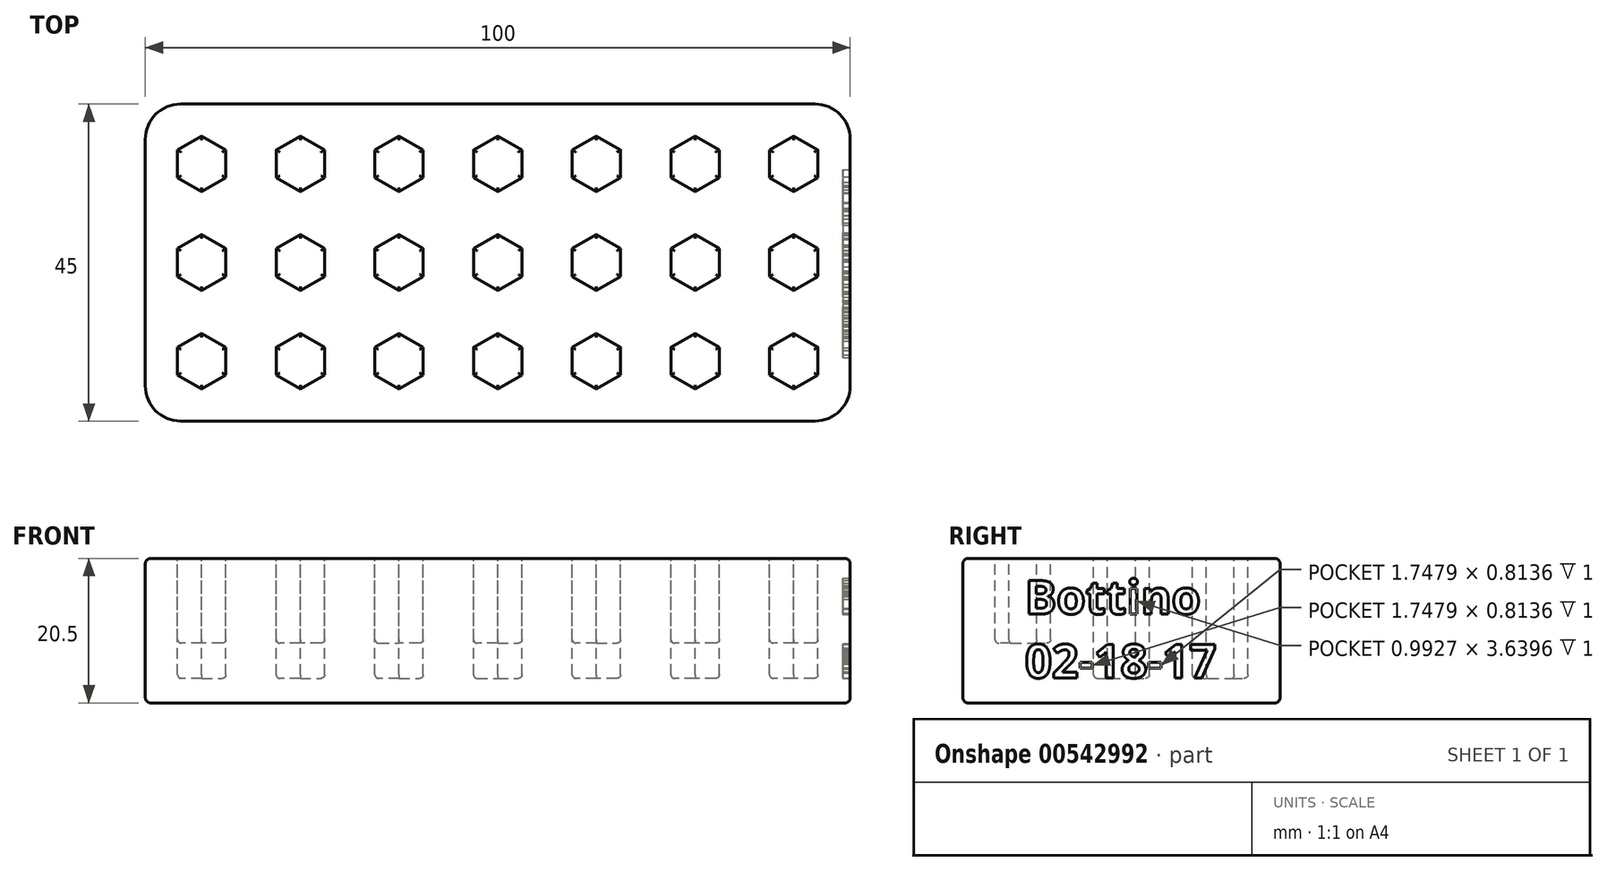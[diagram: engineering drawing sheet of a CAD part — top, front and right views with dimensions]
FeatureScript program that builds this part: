
annotation { "Feature Type Name" : "Feature", "Feature Type Description" : "" }
export const myFeature = defineFeature(function(context is Context, id is Id, definition is map)
    precondition{}
    {
        {
            var Q0;
            Q0=qCreatedBy(makeId("Top.planeOp"),FACE);
            var sketch = newSketch(context, id + "F0", { "sketchPlane" : qUnion([Q0])});
            skLineSegment(sketch, "E0.bottom", {"start": v(45, -22.5) * mm, "end": v(-45, -22.5) * mm});
            skLineSegment(sketch, "E0.top", {"start": v(45, 22.5) * mm, "end": v(-45, 22.5) * mm});
            skLineSegment(sketch, "E0.left", {"start": v(50, -17.5) * mm, "end": v(50, 17.5) * mm});
            skLineSegment(sketch, "E0.right", {"start": v(-50, -17.5) * mm, "end": v(-50, 17.5) * mm});
            skPoint(sketch, "E0.middle", {"position": v(0, 0) * mm});
            skPoint(sketch, "E1.visualSharp", {"position": v(-50, 22.5) * mm});
            skArc(sketch, "E1.filletArc", {"start": v(-45, 22.5) * mm, "mid": v(-48.54, 21.04) * mm, "end": v(-50, 17.5) * mm});
            skPoint(sketch, "E2.visualSharp", {"position": v(50, 22.5) * mm});
            skArc(sketch, "E2.filletArc", {"start": v(50, 17.5) * mm, "mid": v(48.54, 21.04) * mm, "end": v(45, 22.5) * mm});
            skPoint(sketch, "E3.visualSharp", {"position": v(50, -22.5) * mm});
            skArc(sketch, "E3.filletArc", {"start": v(45, -22.5) * mm, "mid": v(48.54, -21.04) * mm, "end": v(50, -17.5) * mm});
            skPoint(sketch, "E4.visualSharp", {"position": v(-50, -22.5) * mm});
            skArc(sketch, "E4.filletArc", {"start": v(-50, -17.5) * mm, "mid": v(-48.54, -21.04) * mm, "end": v(-45, -22.5) * mm});
            skCircle(sketch, "E5.cCircle", {"center": v(0, 0) * mm, "radius": 3.43 * mm, "construction": true});
            skLineSegment(sketch, "E5.0", {"start": v(3.43, 1.98) * mm, "end": v(3.43, -1.98) * mm});
            skLineSegment(sketch, "E5.1", {"start": v(3.43, -1.98) * mm, "end": v(0, -3.95) * mm});
            skLineSegment(sketch, "E5.2", {"start": v(0, -3.95) * mm, "end": v(-3.43, -1.98) * mm});
            skLineSegment(sketch, "E5.3", {"start": v(-3.43, -1.98) * mm, "end": v(-3.43, 1.98) * mm});
            skLineSegment(sketch, "E5.4", {"start": v(-3.43, 1.98) * mm, "end": v(0, 3.95) * mm});
            skLineSegment(sketch, "E5.5", {"start": v(0, 3.95) * mm, "end": v(3.43, 1.98) * mm});
            skPoint(sketch, "E5.0.midPoint", {"position": v(3.43, 0) * mm});
            skLineSegment(sketch, "E6.0.1.0", {"start": v(-3.43, 15.98) * mm, "end": v(0, 17.95) * mm});
            skLineSegment(sketch, "E6.0.1.1", {"start": v(3.43, 12.02) * mm, "end": v(0, 10.05) * mm});
            skLineSegment(sketch, "E6.0.1.2", {"start": v(3.43, 15.98) * mm, "end": v(3.43, 12.02) * mm});
            skPoint(sketch, "E6.0.1.3", {"position": v(3.43, 14) * mm});
            skLineSegment(sketch, "E6.0.1.4", {"start": v(0, 10.05) * mm, "end": v(-3.43, 12.02) * mm});
            skLineSegment(sketch, "E6.0.1.5", {"start": v(-3.43, 12.02) * mm, "end": v(-3.43, 15.98) * mm});
            skCircle(sketch, "E6.0.1.6", {"center": v(0, 14) * mm, "radius": 3.43 * mm, "construction": true});
            skLineSegment(sketch, "E6.0.1.7", {"start": v(0, 17.95) * mm, "end": v(3.43, 15.98) * mm});
            skPoint(sketch, "E6.0.1.8", {"position": v(0, 14) * mm});
            skLineSegment(sketch, "E6.1.0.0", {"start": v(10.58, 1.98) * mm, "end": v(14, 3.95) * mm});
            skLineSegment(sketch, "E6.1.0.1", {"start": v(17.43, -1.98) * mm, "end": v(14, -3.95) * mm});
            skLineSegment(sketch, "E6.1.0.2", {"start": v(17.43, 1.98) * mm, "end": v(17.43, -1.98) * mm});
            skPoint(sketch, "E6.1.0.3", {"position": v(17.43, 0) * mm});
            skLineSegment(sketch, "E6.1.0.4", {"start": v(14, -3.95) * mm, "end": v(10.58, -1.98) * mm});
            skLineSegment(sketch, "E6.1.0.5", {"start": v(10.58, -1.98) * mm, "end": v(10.58, 1.98) * mm});
            skCircle(sketch, "E6.1.0.6", {"center": v(14, 0) * mm, "radius": 3.43 * mm, "construction": true});
            skLineSegment(sketch, "E6.1.0.7", {"start": v(14, 3.95) * mm, "end": v(17.43, 1.98) * mm});
            skPoint(sketch, "E6.1.0.8", {"position": v(14, 0) * mm});
            skLineSegment(sketch, "E6.1.1.0", {"start": v(10.58, 15.98) * mm, "end": v(14, 17.95) * mm});
            skLineSegment(sketch, "E6.1.1.1", {"start": v(17.43, 12.02) * mm, "end": v(14, 10.05) * mm});
            skLineSegment(sketch, "E6.1.1.2", {"start": v(17.43, 15.98) * mm, "end": v(17.43, 12.02) * mm});
            skPoint(sketch, "E6.1.1.3", {"position": v(17.43, 14) * mm});
            skLineSegment(sketch, "E6.1.1.4", {"start": v(14, 10.05) * mm, "end": v(10.58, 12.02) * mm});
            skLineSegment(sketch, "E6.1.1.5", {"start": v(10.58, 12.02) * mm, "end": v(10.58, 15.98) * mm});
            skCircle(sketch, "E6.1.1.6", {"center": v(14, 14) * mm, "radius": 3.43 * mm, "construction": true});
            skLineSegment(sketch, "E6.1.1.7", {"start": v(14, 17.95) * mm, "end": v(17.43, 15.98) * mm});
            skPoint(sketch, "E6.1.1.8", {"position": v(14, 14) * mm});
            skLineSegment(sketch, "E6.2.0.0", {"start": v(24.58, 1.98) * mm, "end": v(28, 3.95) * mm});
            skLineSegment(sketch, "E6.2.0.1", {"start": v(31.43, -1.98) * mm, "end": v(28, -3.95) * mm});
            skLineSegment(sketch, "E6.2.0.2", {"start": v(31.43, 1.98) * mm, "end": v(31.43, -1.98) * mm});
            skPoint(sketch, "E6.2.0.3", {"position": v(31.43, 0) * mm});
            skLineSegment(sketch, "E6.2.0.4", {"start": v(28, -3.95) * mm, "end": v(24.58, -1.98) * mm});
            skLineSegment(sketch, "E6.2.0.5", {"start": v(24.58, -1.98) * mm, "end": v(24.58, 1.98) * mm});
            skCircle(sketch, "E6.2.0.6", {"center": v(28, 0) * mm, "radius": 3.43 * mm, "construction": true});
            skLineSegment(sketch, "E6.2.0.7", {"start": v(28, 3.95) * mm, "end": v(31.43, 1.98) * mm});
            skPoint(sketch, "E6.2.0.8", {"position": v(28, 0) * mm});
            skLineSegment(sketch, "E6.2.1.0", {"start": v(24.58, 15.98) * mm, "end": v(28, 17.95) * mm});
            skLineSegment(sketch, "E6.2.1.1", {"start": v(31.43, 12.02) * mm, "end": v(28, 10.05) * mm});
            skLineSegment(sketch, "E6.2.1.2", {"start": v(31.43, 15.98) * mm, "end": v(31.43, 12.02) * mm});
            skPoint(sketch, "E6.2.1.3", {"position": v(31.43, 14) * mm});
            skLineSegment(sketch, "E6.2.1.4", {"start": v(28, 10.05) * mm, "end": v(24.58, 12.02) * mm});
            skLineSegment(sketch, "E6.2.1.5", {"start": v(24.58, 12.02) * mm, "end": v(24.58, 15.98) * mm});
            skCircle(sketch, "E6.2.1.6", {"center": v(28, 14) * mm, "radius": 3.43 * mm, "construction": true});
            skLineSegment(sketch, "E6.2.1.7", {"start": v(28, 17.95) * mm, "end": v(31.43, 15.98) * mm});
            skPoint(sketch, "E6.2.1.8", {"position": v(28, 14) * mm});
            skLineSegment(sketch, "E6.3.0.0", {"start": v(38.58, 1.98) * mm, "end": v(42, 3.95) * mm});
            skLineSegment(sketch, "E6.3.0.1", {"start": v(45.43, -1.98) * mm, "end": v(42, -3.95) * mm});
            skLineSegment(sketch, "E6.3.0.2", {"start": v(45.43, 1.98) * mm, "end": v(45.43, -1.98) * mm});
            skPoint(sketch, "E6.3.0.3", {"position": v(45.43, 0) * mm});
            skLineSegment(sketch, "E6.3.0.4", {"start": v(42, -3.95) * mm, "end": v(38.58, -1.98) * mm});
            skLineSegment(sketch, "E6.3.0.5", {"start": v(38.58, -1.98) * mm, "end": v(38.58, 1.98) * mm});
            skCircle(sketch, "E6.3.0.6", {"center": v(42, 0) * mm, "radius": 3.43 * mm, "construction": true});
            skLineSegment(sketch, "E6.3.0.7", {"start": v(42, 3.95) * mm, "end": v(45.43, 1.98) * mm});
            skPoint(sketch, "E6.3.0.8", {"position": v(42, 0) * mm});
            skLineSegment(sketch, "E6.3.1.0", {"start": v(38.58, 15.98) * mm, "end": v(42, 17.95) * mm});
            skLineSegment(sketch, "E6.3.1.1", {"start": v(45.43, 12.02) * mm, "end": v(42, 10.05) * mm});
            skLineSegment(sketch, "E6.3.1.2", {"start": v(45.43, 15.98) * mm, "end": v(45.43, 12.02) * mm});
            skPoint(sketch, "E6.3.1.3", {"position": v(45.43, 14) * mm});
            skLineSegment(sketch, "E6.3.1.4", {"start": v(42, 10.05) * mm, "end": v(38.58, 12.02) * mm});
            skLineSegment(sketch, "E6.3.1.5", {"start": v(38.58, 12.02) * mm, "end": v(38.58, 15.98) * mm});
            skCircle(sketch, "E6.3.1.6", {"center": v(42, 14) * mm, "radius": 3.43 * mm, "construction": true});
            skLineSegment(sketch, "E6.3.1.7", {"start": v(42, 17.95) * mm, "end": v(45.43, 15.98) * mm});
            skPoint(sketch, "E6.3.1.8", {"position": v(42, 14) * mm});
            skLineSegment(sketch, "E6.direction1", {"start": v(-3.43, -1.98) * mm, "end": v(10.58, -1.98) * mm, "construction": true});
            skLineSegment(sketch, "E6.direction2", {"start": v(-3.43, -1.98) * mm, "end": v(-3.43, 12.02) * mm, "construction": true});
            skLineSegment(sketch, "E7", {"start": v(0, 36.48) * mm, "end": v(0, -38.23) * mm, "construction": true});
            skLineSegment(sketch, "E8.MirrorCS", {"start": v(-10.58, 15.98) * mm, "end": v(-14, 17.95) * mm});
            skLineSegment(sketch, "E9.MirrorCS", {"start": v(-14, 17.95) * mm, "end": v(-17.43, 15.98) * mm});
            skLineSegment(sketch, "E10.MirrorCS", {"start": v(-17.43, 15.98) * mm, "end": v(-17.43, 12.02) * mm});
            skLineSegment(sketch, "E11.MirrorCS", {"start": v(-17.43, 12.02) * mm, "end": v(-14, 10.05) * mm});
            skLineSegment(sketch, "E12.MirrorCS", {"start": v(-14, 10.05) * mm, "end": v(-10.58, 12.02) * mm});
            skLineSegment(sketch, "E13.MirrorCS", {"start": v(-10.58, 12.02) * mm, "end": v(-10.58, 15.98) * mm});
            skLineSegment(sketch, "E14.MirrorCS", {"start": v(-24.58, 12.02) * mm, "end": v(-24.58, 15.98) * mm});
            skLineSegment(sketch, "E15.MirrorCS", {"start": v(-24.58, 15.98) * mm, "end": v(-28, 17.95) * mm});
            skLineSegment(sketch, "E16.MirrorCS", {"start": v(-28, 17.95) * mm, "end": v(-31.43, 15.98) * mm});
            skLineSegment(sketch, "E17.MirrorCS", {"start": v(-31.43, 15.98) * mm, "end": v(-31.43, 12.02) * mm});
            skLineSegment(sketch, "E18.MirrorCS", {"start": v(-31.43, 12.02) * mm, "end": v(-28, 10.05) * mm});
            skLineSegment(sketch, "E19.MirrorCS", {"start": v(-28, 3.95) * mm, "end": v(-31.43, 1.98) * mm});
            skLineSegment(sketch, "E20.MirrorCS", {"start": v(-24.58, 1.98) * mm, "end": v(-28, 3.95) * mm});
            skLineSegment(sketch, "E21.MirrorCS", {"start": v(-24.58, -1.98) * mm, "end": v(-24.58, 1.98) * mm});
            skLineSegment(sketch, "E22.MirrorCS", {"start": v(-28, -3.95) * mm, "end": v(-24.58, -1.98) * mm});
            skLineSegment(sketch, "E23.MirrorCS", {"start": v(-31.43, -1.98) * mm, "end": v(-28, -3.95) * mm});
            skLineSegment(sketch, "E24.MirrorCS", {"start": v(-28, 10.05) * mm, "end": v(-24.58, 12.02) * mm});
            skLineSegment(sketch, "E25.MirrorCS", {"start": v(-31.43, 1.98) * mm, "end": v(-31.43, -1.98) * mm});
            skLineSegment(sketch, "E26.MirrorCS", {"start": v(-38.58, 15.98) * mm, "end": v(-42, 17.95) * mm});
            skLineSegment(sketch, "E27.MirrorCS", {"start": v(-42, 17.95) * mm, "end": v(-45.43, 15.98) * mm});
            skLineSegment(sketch, "E28.MirrorCS", {"start": v(-45.43, 15.98) * mm, "end": v(-45.43, 12.02) * mm});
            skLineSegment(sketch, "E29.MirrorCS", {"start": v(-45.43, 12.02) * mm, "end": v(-42, 10.05) * mm});
            skLineSegment(sketch, "E30.MirrorCS", {"start": v(-42, 10.05) * mm, "end": v(-38.58, 12.02) * mm});
            skLineSegment(sketch, "E31.MirrorCS", {"start": v(-38.58, 12.02) * mm, "end": v(-38.58, 15.98) * mm});
            skLineSegment(sketch, "E32.MirrorCS", {"start": v(-38.58, 1.98) * mm, "end": v(-42, 3.95) * mm});
            skLineSegment(sketch, "E33.MirrorCS", {"start": v(-42, 3.95) * mm, "end": v(-45.43, 1.98) * mm});
            skLineSegment(sketch, "E34.MirrorCS", {"start": v(-45.43, 1.98) * mm, "end": v(-45.43, -1.98) * mm});
            skLineSegment(sketch, "E35.MirrorCS", {"start": v(-45.43, -1.98) * mm, "end": v(-42, -3.95) * mm});
            skLineSegment(sketch, "E36.MirrorCS", {"start": v(-42, -3.95) * mm, "end": v(-38.58, -1.98) * mm});
            skLineSegment(sketch, "E37.MirrorCS", {"start": v(-38.58, -1.98) * mm, "end": v(-38.58, 1.98) * mm});
            skLineSegment(sketch, "E38.MirrorCS", {"start": v(-10.58, 1.98) * mm, "end": v(-14, 3.95) * mm});
            skLineSegment(sketch, "E39.MirrorCS", {"start": v(-14, 3.95) * mm, "end": v(-17.43, 1.98) * mm});
            skLineSegment(sketch, "E40.MirrorCS", {"start": v(-17.43, 1.98) * mm, "end": v(-17.43, -1.98) * mm});
            skLineSegment(sketch, "E41.MirrorCS", {"start": v(-17.43, -1.98) * mm, "end": v(-14, -3.95) * mm});
            skLineSegment(sketch, "E42.MirrorCS", {"start": v(-14, -3.95) * mm, "end": v(-10.58, -1.98) * mm});
            skLineSegment(sketch, "E43.MirrorCS", {"start": v(-10.58, -1.98) * mm, "end": v(-10.58, 1.98) * mm});
            skLineSegment(sketch, "E44", {"start": v(-62.75, 0) * mm, "end": v(58.2, 0) * mm, "construction": true});
            skLineSegment(sketch, "E45.MirrorCS", {"start": v(-31.43, -12.02) * mm, "end": v(-28, -10.05) * mm});
            skLineSegment(sketch, "E46.MirrorCS", {"start": v(-45.43, -12.02) * mm, "end": v(-42, -10.05) * mm});
            skLineSegment(sketch, "E47.MirrorCS", {"start": v(-28, -17.95) * mm, "end": v(-31.43, -15.98) * mm});
            skLineSegment(sketch, "E48.MirrorCS", {"start": v(-10.58, -15.98) * mm, "end": v(-14, -17.95) * mm});
            skLineSegment(sketch, "E49.MirrorCS", {"start": v(-38.58, -12.02) * mm, "end": v(-38.58, -15.98) * mm});
            skLineSegment(sketch, "E50.MirrorCS", {"start": v(-42, -10.05) * mm, "end": v(-38.58, -12.02) * mm});
            skLineSegment(sketch, "E51.MirrorCS", {"start": v(-31.43, -15.98) * mm, "end": v(-31.43, -12.02) * mm});
            skLineSegment(sketch, "E52.MirrorCS", {"start": v(-45.43, -15.98) * mm, "end": v(-45.43, -12.02) * mm});
            skLineSegment(sketch, "E53.MirrorCS", {"start": v(-24.58, -15.98) * mm, "end": v(-28, -17.95) * mm});
            skLineSegment(sketch, "E54.MirrorCS", {"start": v(-38.58, -15.98) * mm, "end": v(-42, -17.95) * mm});
            skLineSegment(sketch, "E55.MirrorCS", {"start": v(-14, -10.05) * mm, "end": v(-10.58, -12.02) * mm});
            skLineSegment(sketch, "E56.MirrorCS", {"start": v(-10.58, -12.02) * mm, "end": v(-10.58, -15.98) * mm});
            skLineSegment(sketch, "E57.MirrorCS", {"start": v(-28, -10.05) * mm, "end": v(-24.58, -12.02) * mm});
            skLineSegment(sketch, "E58.MirrorCS", {"start": v(-17.43, -12.02) * mm, "end": v(-14, -10.05) * mm});
            skLineSegment(sketch, "E59.MirrorCS", {"start": v(-17.43, -15.98) * mm, "end": v(-17.43, -12.02) * mm});
            skLineSegment(sketch, "E60.MirrorCS", {"start": v(-14, -17.95) * mm, "end": v(-17.43, -15.98) * mm});
            skLineSegment(sketch, "E61.MirrorCS", {"start": v(-42, -17.95) * mm, "end": v(-45.43, -15.98) * mm});
            skLineSegment(sketch, "E62.MirrorCS", {"start": v(-24.58, -12.02) * mm, "end": v(-24.58, -15.98) * mm});
            skLineSegment(sketch, "E63.MirrorCS", {"start": v(-3.43, -15.98) * mm, "end": v(0, -17.95) * mm});
            skLineSegment(sketch, "E64.MirrorCS", {"start": v(0, -17.95) * mm, "end": v(3.43, -15.98) * mm});
            skLineSegment(sketch, "E65.MirrorCS", {"start": v(3.43, -15.98) * mm, "end": v(3.43, -12.02) * mm});
            skLineSegment(sketch, "E66.MirrorCS", {"start": v(3.43, -12.02) * mm, "end": v(0, -10.05) * mm});
            skLineSegment(sketch, "E67.MirrorCS", {"start": v(0, -10.05) * mm, "end": v(-3.43, -12.02) * mm});
            skLineSegment(sketch, "E68.MirrorCS", {"start": v(-3.43, -12.02) * mm, "end": v(-3.43, -15.98) * mm});
            skLineSegment(sketch, "E69.MirrorCS", {"start": v(10.58, -15.98) * mm, "end": v(14, -17.95) * mm});
            skLineSegment(sketch, "E70.MirrorCS", {"start": v(14, -17.95) * mm, "end": v(17.43, -15.98) * mm});
            skLineSegment(sketch, "E71.MirrorCS", {"start": v(17.43, -15.98) * mm, "end": v(17.43, -12.02) * mm});
            skLineSegment(sketch, "E72.MirrorCS", {"start": v(17.43, -12.02) * mm, "end": v(14, -10.05) * mm});
            skLineSegment(sketch, "E73.MirrorCS", {"start": v(14, -10.05) * mm, "end": v(10.58, -12.02) * mm});
            skLineSegment(sketch, "E74.MirrorCS", {"start": v(10.58, -12.02) * mm, "end": v(10.58, -15.98) * mm});
            skLineSegment(sketch, "E75.MirrorCS", {"start": v(28, -10.05) * mm, "end": v(24.58, -12.02) * mm});
            skLineSegment(sketch, "E76.MirrorCS", {"start": v(24.58, -12.02) * mm, "end": v(24.58, -15.98) * mm});
            skLineSegment(sketch, "E77.MirrorCS", {"start": v(24.58, -15.98) * mm, "end": v(28, -17.95) * mm});
            skLineSegment(sketch, "E78.MirrorCS", {"start": v(28, -17.95) * mm, "end": v(31.43, -15.98) * mm});
            skLineSegment(sketch, "E79.MirrorCS", {"start": v(31.43, -15.98) * mm, "end": v(31.43, -12.02) * mm});
            skLineSegment(sketch, "E80.MirrorCS", {"start": v(31.43, -12.02) * mm, "end": v(28, -10.05) * mm});
            skLineSegment(sketch, "E81.MirrorCS", {"start": v(42, -10.05) * mm, "end": v(38.58, -12.02) * mm});
            skLineSegment(sketch, "E82.MirrorCS", {"start": v(38.58, -12.02) * mm, "end": v(38.58, -15.98) * mm});
            skLineSegment(sketch, "E83.MirrorCS", {"start": v(38.58, -15.98) * mm, "end": v(42, -17.95) * mm});
            skLineSegment(sketch, "E84.MirrorCS", {"start": v(42, -17.95) * mm, "end": v(45.43, -15.98) * mm});
            skLineSegment(sketch, "E85.MirrorCS", {"start": v(45.43, -15.98) * mm, "end": v(45.43, -12.02) * mm});
            skLineSegment(sketch, "E86.MirrorCS", {"start": v(45.43, -12.02) * mm, "end": v(42, -10.05) * mm});
            skSolve(sketch);
        }
        {
            var Q0;
            Q0=qCreatedBy(makeId("Top.planeOp"),FACE);
            var sketch = newSketch(context, id + "F1", { "sketchPlane" : qUnion([Q0])});
            skArc(sketch, "E87.0", {"start": v(-45, 22.5) * mm, "mid": v(-48.54, 21.04) * mm, "end": v(-50, 17.5) * mm});
            skLineSegment(sketch, "E88.0", {"start": v(45, 22.5) * mm, "end": v(-45, 22.5) * mm});
            skArc(sketch, "E89.0", {"start": v(50, 17.5) * mm, "mid": v(48.54, 21.04) * mm, "end": v(45, 22.5) * mm});
            skLineSegment(sketch, "E90.0", {"start": v(50, -17.5) * mm, "end": v(50, 17.5) * mm});
            skArc(sketch, "E91.0", {"start": v(45, -22.5) * mm, "mid": v(48.54, -21.04) * mm, "end": v(50, -17.5) * mm});
            skLineSegment(sketch, "E92.0", {"start": v(45, -22.5) * mm, "end": v(-45, -22.5) * mm});
            skArc(sketch, "E93.0", {"start": v(-50, -17.5) * mm, "mid": v(-48.54, -21.04) * mm, "end": v(-45, -22.5) * mm});
            skLineSegment(sketch, "E94.0", {"start": v(-50, -17.5) * mm, "end": v(-50, 17.5) * mm});
            skSolve(sketch);
        }
        {
            var Q0;
            Q0 = qSketchRegion(id + "F1", true);
            extrude(context, id + "F2", {"entities" : qUnion([Q0]), "oppositeDirection" : true, "depth" : 20.5 * mm, "offsetDistance" : 25 * mm});
        }
        {
            var Q0;
            Q0=makeQuery(id+"F0.imprint","IMPRINT",FACE,{"disambiguationData":[TD([[makeQuery(id+"F0.imprint","IMPRINT",EDGE,{"derivedFrom":sQuery(id+"F0.wireOp",EDGE,"E46.MirrorCS")}),-1.0]])]});
            var Q1;
            Q1=makeQuery(id+"F0.imprint","IMPRINT",FACE,{"disambiguationData":[TD([[makeQuery(id+"F0.imprint","IMPRINT",EDGE,{"derivedFrom":sQuery(id+"F0.wireOp",EDGE,"E47.MirrorCS")}),-1.0]])]});
            var Q2;
            Q2=makeQuery(id+"F0.imprint","IMPRINT",FACE,{"disambiguationData":[TD([[makeQuery(id+"F0.imprint","IMPRINT",EDGE,{"derivedFrom":sQuery(id+"F0.wireOp",EDGE,"E48.MirrorCS")}),-1.0]])]});
            var Q3;
            Q3=makeQuery(id+"F0.imprint","IMPRINT",FACE,{"disambiguationData":[TD([[makeQuery(id+"F0.imprint","IMPRINT",EDGE,{"derivedFrom":sQuery(id+"F0.wireOp",EDGE,"E63.MirrorCS")}),1.0]])]});
            var Q4;
            Q4=makeQuery(id+"F0.imprint","IMPRINT",FACE,{"disambiguationData":[TD([[makeQuery(id+"F0.imprint","IMPRINT",EDGE,{"derivedFrom":sQuery(id+"F0.wireOp",EDGE,"E69.MirrorCS")}),1.0]])]});
            var Q5;
            Q5=makeQuery(id+"F0.imprint","IMPRINT",FACE,{"disambiguationData":[TD([[makeQuery(id+"F0.imprint","IMPRINT",EDGE,{"derivedFrom":sQuery(id+"F0.wireOp",EDGE,"E75.MirrorCS")}),1.0]])]});
            var Q6;
            Q6=makeQuery(id+"F0.imprint","IMPRINT",FACE,{"disambiguationData":[TD([[makeQuery(id+"F0.imprint","IMPRINT",EDGE,{"derivedFrom":sQuery(id+"F0.wireOp",EDGE,"E81.MirrorCS")}),1.0]])]});
            extrude(context, id + "F3", {"entities" : qUnion([Q0, Q1, Q2, Q3, Q4, Q5, Q6]), "operationType" : NewBodyOperationType.REMOVE, "oppositeDirection" : true, "depth" : 12 * mm, "offsetDistance" : 25 * mm});
        }
        {
            var Q0;
            Q0=makeQuery(id+"F0.imprint","IMPRINT",FACE,{"disambiguationData":[TD([[makeQuery(id+"F0.imprint","IMPRINT",EDGE,{"derivedFrom":sQuery(id+"F0.wireOp",EDGE,"E26.MirrorCS")}),1.0]])]});
            var Q1;
            Q1=makeQuery(id+"F0.imprint","IMPRINT",FACE,{"disambiguationData":[TD([[makeQuery(id+"F0.imprint","IMPRINT",EDGE,{"derivedFrom":sQuery(id+"F0.wireOp",EDGE,"E14.MirrorCS")}),1.0]])]});
            var Q2;
            Q2=makeQuery(id+"F0.imprint","IMPRINT",FACE,{"disambiguationData":[TD([[makeQuery(id+"F0.imprint","IMPRINT",EDGE,{"derivedFrom":sQuery(id+"F0.wireOp",EDGE,"E8.MirrorCS")}),1.0]])]});
            var Q3;
            Q3=makeQuery(id+"F0.imprint","IMPRINT",FACE,{"disambiguationData":[TD([[makeQuery(id+"F0.imprint","IMPRINT",EDGE,{"derivedFrom":sQuery(id+"F0.wireOp",EDGE,"E6.0.1.0")}),-1.0]])]});
            var Q4;
            Q4=makeQuery(id+"F0.imprint","IMPRINT",FACE,{"disambiguationData":[TD([[makeQuery(id+"F0.imprint","IMPRINT",EDGE,{"derivedFrom":sQuery(id+"F0.wireOp",EDGE,"E6.1.1.0")}),-1.0]])]});
            var Q5;
            Q5=makeQuery(id+"F0.imprint","IMPRINT",FACE,{"disambiguationData":[TD([[makeQuery(id+"F0.imprint","IMPRINT",EDGE,{"derivedFrom":sQuery(id+"F0.wireOp",EDGE,"E6.2.1.0")}),-1.0]])]});
            var Q6;
            Q6=makeQuery(id+"F0.imprint","IMPRINT",FACE,{"disambiguationData":[TD([[makeQuery(id+"F0.imprint","IMPRINT",EDGE,{"derivedFrom":sQuery(id+"F0.wireOp",EDGE,"E6.3.1.0")}),-1.0]])]});
            var Q7;
            Q7=makeQuery(id+"F0.imprint","IMPRINT",FACE,{"disambiguationData":[TD([[makeQuery(id+"F0.imprint","IMPRINT",EDGE,{"derivedFrom":sQuery(id+"F0.wireOp",EDGE,"E6.3.0.0")}),-1.0]])]});
            var Q8;
            Q8=makeQuery(id+"F0.imprint","IMPRINT",FACE,{"disambiguationData":[TD([[makeQuery(id+"F0.imprint","IMPRINT",EDGE,{"derivedFrom":sQuery(id+"F0.wireOp",EDGE,"E6.2.0.0")}),-1.0]])]});
            var Q9;
            Q9=makeQuery(id+"F0.imprint","IMPRINT",FACE,{"disambiguationData":[TD([[makeQuery(id+"F0.imprint","IMPRINT",EDGE,{"derivedFrom":sQuery(id+"F0.wireOp",EDGE,"E6.1.0.0")}),-1.0]])]});
            var Q10;
            Q10=makeQuery(id+"F0.imprint","IMPRINT",FACE,{"disambiguationData":[TD([[makeQuery(id+"F0.imprint","IMPRINT",EDGE,{"derivedFrom":sQuery(id+"F0.wireOp",EDGE,"E5.0")}),-1.0]])]});
            var Q11;
            Q11=makeQuery(id+"F0.imprint","IMPRINT",FACE,{"disambiguationData":[TD([[makeQuery(id+"F0.imprint","IMPRINT",EDGE,{"derivedFrom":sQuery(id+"F0.wireOp",EDGE,"E38.MirrorCS")}),1.0]])]});
            var Q12;
            Q12=makeQuery(id+"F0.imprint","IMPRINT",FACE,{"disambiguationData":[TD([[makeQuery(id+"F0.imprint","IMPRINT",EDGE,{"derivedFrom":sQuery(id+"F0.wireOp",EDGE,"E19.MirrorCS")}),1.0]])]});
            var Q13;
            Q13=makeQuery(id+"F0.imprint","IMPRINT",FACE,{"disambiguationData":[TD([[makeQuery(id+"F0.imprint","IMPRINT",EDGE,{"derivedFrom":sQuery(id+"F0.wireOp",EDGE,"E32.MirrorCS")}),1.0]])]});
            extrude(context, id + "F4", {"entities" : qUnion([Q0, Q1, Q2, Q3, Q4, Q5, Q6, Q7, Q8, Q9, Q10, Q11, Q12, Q13]), "operationType" : NewBodyOperationType.REMOVE, "oppositeDirection" : true, "depth" : 17 * mm, "offsetDistance" : 25 * mm});
        }
        {
            var Q0;
            Q0=makeQuery(id+"F4.boolean.opBoolean","COPY",FACE,{"derivedFrom":makeQuery(id+"F4.opExtrude","CAP_FACE",FACE,{"disambiguationData":[OSD([sQuery(id+"F0.wireOp",EDGE,"E26.MirrorCS"),sQuery(id+"F0.wireOp",EDGE,"E27.MirrorCS"),sQuery(id+"F0.wireOp",EDGE,"E28.MirrorCS"),sQuery(id+"F0.wireOp",EDGE,"E29.MirrorCS"),sQuery(id+"F0.wireOp",EDGE,"E30.MirrorCS"),sQuery(id+"F0.wireOp",EDGE,"E31.MirrorCS")])],"isStart":false})});
            var Q1;
            Q1=makeQuery(id+"F4.boolean.opBoolean","COPY",FACE,{"derivedFrom":makeQuery(id+"F4.opExtrude","CAP_FACE",FACE,{"disambiguationData":[OSD([sQuery(id+"F0.wireOp",EDGE,"E14.MirrorCS"),sQuery(id+"F0.wireOp",EDGE,"E15.MirrorCS"),sQuery(id+"F0.wireOp",EDGE,"E16.MirrorCS"),sQuery(id+"F0.wireOp",EDGE,"E17.MirrorCS"),sQuery(id+"F0.wireOp",EDGE,"E18.MirrorCS"),sQuery(id+"F0.wireOp",EDGE,"E24.MirrorCS")])],"isStart":false})});
            var Q2;
            Q2=makeQuery(id+"F4.boolean.opBoolean","COPY",FACE,{"derivedFrom":makeQuery(id+"F4.opExtrude","CAP_FACE",FACE,{"disambiguationData":[OSD([sQuery(id+"F0.wireOp",EDGE,"E8.MirrorCS"),sQuery(id+"F0.wireOp",EDGE,"E9.MirrorCS"),sQuery(id+"F0.wireOp",EDGE,"E10.MirrorCS"),sQuery(id+"F0.wireOp",EDGE,"E11.MirrorCS"),sQuery(id+"F0.wireOp",EDGE,"E12.MirrorCS"),sQuery(id+"F0.wireOp",EDGE,"E13.MirrorCS")])],"isStart":false})});
            var Q3;
            Q3=makeQuery(id+"F4.boolean.opBoolean","COPY",FACE,{"derivedFrom":makeQuery(id+"F4.opExtrude","CAP_FACE",FACE,{"disambiguationData":[OSD([sQuery(id+"F0.wireOp",EDGE,"E6.0.1.0"),sQuery(id+"F0.wireOp",EDGE,"E6.0.1.1"),sQuery(id+"F0.wireOp",EDGE,"E6.0.1.2"),sQuery(id+"F0.wireOp",EDGE,"E6.0.1.4"),sQuery(id+"F0.wireOp",EDGE,"E6.0.1.5"),sQuery(id+"F0.wireOp",EDGE,"E6.0.1.7")])],"isStart":false})});
            var Q4;
            Q4=makeQuery(id+"F4.boolean.opBoolean","COPY",FACE,{"derivedFrom":makeQuery(id+"F4.opExtrude","CAP_FACE",FACE,{"disambiguationData":[OSD([sQuery(id+"F0.wireOp",EDGE,"E6.1.1.0"),sQuery(id+"F0.wireOp",EDGE,"E6.1.1.1"),sQuery(id+"F0.wireOp",EDGE,"E6.1.1.2"),sQuery(id+"F0.wireOp",EDGE,"E6.1.1.4"),sQuery(id+"F0.wireOp",EDGE,"E6.1.1.5"),sQuery(id+"F0.wireOp",EDGE,"E6.1.1.7")])],"isStart":false})});
            var Q5;
            Q5=makeQuery(id+"F4.boolean.opBoolean","COPY",FACE,{"derivedFrom":makeQuery(id+"F4.opExtrude","CAP_FACE",FACE,{"disambiguationData":[OSD([sQuery(id+"F0.wireOp",EDGE,"E6.2.1.0"),sQuery(id+"F0.wireOp",EDGE,"E6.2.1.1"),sQuery(id+"F0.wireOp",EDGE,"E6.2.1.2"),sQuery(id+"F0.wireOp",EDGE,"E6.2.1.4"),sQuery(id+"F0.wireOp",EDGE,"E6.2.1.5"),sQuery(id+"F0.wireOp",EDGE,"E6.2.1.7")])],"isStart":false})});
            var Q6;
            Q6=makeQuery(id+"F4.boolean.opBoolean","COPY",FACE,{"derivedFrom":makeQuery(id+"F4.opExtrude","CAP_FACE",FACE,{"disambiguationData":[OSD([sQuery(id+"F0.wireOp",EDGE,"E6.3.1.0"),sQuery(id+"F0.wireOp",EDGE,"E6.3.1.1"),sQuery(id+"F0.wireOp",EDGE,"E6.3.1.2"),sQuery(id+"F0.wireOp",EDGE,"E6.3.1.4"),sQuery(id+"F0.wireOp",EDGE,"E6.3.1.5"),sQuery(id+"F0.wireOp",EDGE,"E6.3.1.7")])],"isStart":false})});
            var Q7;
            Q7=makeQuery(id+"F4.boolean.opBoolean","COPY",FACE,{"derivedFrom":makeQuery(id+"F4.opExtrude","CAP_FACE",FACE,{"disambiguationData":[OSD([sQuery(id+"F0.wireOp",EDGE,"E6.3.0.0"),sQuery(id+"F0.wireOp",EDGE,"E6.3.0.1"),sQuery(id+"F0.wireOp",EDGE,"E6.3.0.2"),sQuery(id+"F0.wireOp",EDGE,"E6.3.0.4"),sQuery(id+"F0.wireOp",EDGE,"E6.3.0.5"),sQuery(id+"F0.wireOp",EDGE,"E6.3.0.7")])],"isStart":false})});
            var Q8;
            Q8=makeQuery(id+"F4.boolean.opBoolean","COPY",FACE,{"derivedFrom":makeQuery(id+"F4.opExtrude","CAP_FACE",FACE,{"disambiguationData":[OSD([sQuery(id+"F0.wireOp",EDGE,"E6.2.0.0"),sQuery(id+"F0.wireOp",EDGE,"E6.2.0.1"),sQuery(id+"F0.wireOp",EDGE,"E6.2.0.2"),sQuery(id+"F0.wireOp",EDGE,"E6.2.0.4"),sQuery(id+"F0.wireOp",EDGE,"E6.2.0.5"),sQuery(id+"F0.wireOp",EDGE,"E6.2.0.7")])],"isStart":false})});
            var Q9;
            Q9=makeQuery(id+"F4.boolean.opBoolean","COPY",FACE,{"derivedFrom":makeQuery(id+"F4.opExtrude","CAP_FACE",FACE,{"disambiguationData":[OSD([sQuery(id+"F0.wireOp",EDGE,"E6.1.0.0"),sQuery(id+"F0.wireOp",EDGE,"E6.1.0.1"),sQuery(id+"F0.wireOp",EDGE,"E6.1.0.2"),sQuery(id+"F0.wireOp",EDGE,"E6.1.0.4"),sQuery(id+"F0.wireOp",EDGE,"E6.1.0.5"),sQuery(id+"F0.wireOp",EDGE,"E6.1.0.7")])],"isStart":false})});
            var Q10;
            Q10=makeQuery(id+"F4.boolean.opBoolean","COPY",FACE,{"derivedFrom":makeQuery(id+"F4.opExtrude","CAP_FACE",FACE,{"disambiguationData":[OSD([sQuery(id+"F0.wireOp",EDGE,"E5.0"),sQuery(id+"F0.wireOp",EDGE,"E5.1"),sQuery(id+"F0.wireOp",EDGE,"E5.2"),sQuery(id+"F0.wireOp",EDGE,"E5.3"),sQuery(id+"F0.wireOp",EDGE,"E5.4"),sQuery(id+"F0.wireOp",EDGE,"E5.5")])],"isStart":false})});
            var Q11;
            Q11=makeQuery(id+"F4.boolean.opBoolean","COPY",FACE,{"derivedFrom":makeQuery(id+"F4.opExtrude","CAP_FACE",FACE,{"disambiguationData":[OSD([sQuery(id+"F0.wireOp",EDGE,"E38.MirrorCS"),sQuery(id+"F0.wireOp",EDGE,"E39.MirrorCS"),sQuery(id+"F0.wireOp",EDGE,"E40.MirrorCS"),sQuery(id+"F0.wireOp",EDGE,"E41.MirrorCS"),sQuery(id+"F0.wireOp",EDGE,"E42.MirrorCS"),sQuery(id+"F0.wireOp",EDGE,"E43.MirrorCS")])],"isStart":false})});
            var Q12;
            Q12=makeQuery(id+"F4.boolean.opBoolean","COPY",FACE,{"derivedFrom":makeQuery(id+"F4.opExtrude","CAP_FACE",FACE,{"disambiguationData":[OSD([sQuery(id+"F0.wireOp",EDGE,"E19.MirrorCS"),sQuery(id+"F0.wireOp",EDGE,"E20.MirrorCS"),sQuery(id+"F0.wireOp",EDGE,"E22.MirrorCS"),sQuery(id+"F0.wireOp",EDGE,"E23.MirrorCS"),sQuery(id+"F0.wireOp",EDGE,"E21.MirrorCS"),sQuery(id+"F0.wireOp",EDGE,"E25.MirrorCS")])],"isStart":false})});
            var Q13;
            Q13=makeQuery(id+"F4.boolean.opBoolean","COPY",FACE,{"derivedFrom":makeQuery(id+"F4.opExtrude","CAP_FACE",FACE,{"disambiguationData":[OSD([sQuery(id+"F0.wireOp",EDGE,"E32.MirrorCS"),sQuery(id+"F0.wireOp",EDGE,"E33.MirrorCS"),sQuery(id+"F0.wireOp",EDGE,"E34.MirrorCS"),sQuery(id+"F0.wireOp",EDGE,"E35.MirrorCS"),sQuery(id+"F0.wireOp",EDGE,"E36.MirrorCS"),sQuery(id+"F0.wireOp",EDGE,"E37.MirrorCS")])],"isStart":false})});
            var Q14;
            Q14=makeQuery(id+"F3.boolean.opBoolean","COPY",FACE,{"derivedFrom":makeQuery(id+"F3.opExtrude","CAP_FACE",FACE,{"disambiguationData":[OSD([sQuery(id+"F0.wireOp",EDGE,"E46.MirrorCS"),sQuery(id+"F0.wireOp",EDGE,"E49.MirrorCS"),sQuery(id+"F0.wireOp",EDGE,"E50.MirrorCS"),sQuery(id+"F0.wireOp",EDGE,"E52.MirrorCS"),sQuery(id+"F0.wireOp",EDGE,"E54.MirrorCS"),sQuery(id+"F0.wireOp",EDGE,"E61.MirrorCS")])],"isStart":false})});
            var Q15;
            Q15=makeQuery(id+"F3.boolean.opBoolean","COPY",FACE,{"derivedFrom":makeQuery(id+"F3.opExtrude","CAP_FACE",FACE,{"disambiguationData":[OSD([sQuery(id+"F0.wireOp",EDGE,"E47.MirrorCS"),sQuery(id+"F0.wireOp",EDGE,"E51.MirrorCS"),sQuery(id+"F0.wireOp",EDGE,"E45.MirrorCS"),sQuery(id+"F0.wireOp",EDGE,"E53.MirrorCS"),sQuery(id+"F0.wireOp",EDGE,"E57.MirrorCS"),sQuery(id+"F0.wireOp",EDGE,"E62.MirrorCS")])],"isStart":false})});
            var Q16;
            Q16=makeQuery(id+"F3.boolean.opBoolean","COPY",FACE,{"derivedFrom":makeQuery(id+"F3.opExtrude","CAP_FACE",FACE,{"disambiguationData":[OSD([sQuery(id+"F0.wireOp",EDGE,"E48.MirrorCS"),sQuery(id+"F0.wireOp",EDGE,"E55.MirrorCS"),sQuery(id+"F0.wireOp",EDGE,"E56.MirrorCS"),sQuery(id+"F0.wireOp",EDGE,"E58.MirrorCS"),sQuery(id+"F0.wireOp",EDGE,"E59.MirrorCS"),sQuery(id+"F0.wireOp",EDGE,"E60.MirrorCS")])],"isStart":false})});
            var Q17;
            Q17=makeQuery(id+"F3.boolean.opBoolean","COPY",FACE,{"derivedFrom":makeQuery(id+"F3.opExtrude","CAP_FACE",FACE,{"disambiguationData":[OSD([sQuery(id+"F0.wireOp",EDGE,"E63.MirrorCS"),sQuery(id+"F0.wireOp",EDGE,"E64.MirrorCS"),sQuery(id+"F0.wireOp",EDGE,"E65.MirrorCS"),sQuery(id+"F0.wireOp",EDGE,"E66.MirrorCS"),sQuery(id+"F0.wireOp",EDGE,"E67.MirrorCS"),sQuery(id+"F0.wireOp",EDGE,"E68.MirrorCS")])],"isStart":false})});
            var Q18;
            Q18=makeQuery(id+"F3.boolean.opBoolean","COPY",FACE,{"derivedFrom":makeQuery(id+"F3.opExtrude","CAP_FACE",FACE,{"disambiguationData":[OSD([sQuery(id+"F0.wireOp",EDGE,"E69.MirrorCS"),sQuery(id+"F0.wireOp",EDGE,"E70.MirrorCS"),sQuery(id+"F0.wireOp",EDGE,"E71.MirrorCS"),sQuery(id+"F0.wireOp",EDGE,"E72.MirrorCS"),sQuery(id+"F0.wireOp",EDGE,"E73.MirrorCS"),sQuery(id+"F0.wireOp",EDGE,"E74.MirrorCS")])],"isStart":false})});
            var Q19;
            Q19=makeQuery(id+"F3.boolean.opBoolean","COPY",FACE,{"derivedFrom":makeQuery(id+"F3.opExtrude","CAP_FACE",FACE,{"disambiguationData":[OSD([sQuery(id+"F0.wireOp",EDGE,"E75.MirrorCS"),sQuery(id+"F0.wireOp",EDGE,"E76.MirrorCS"),sQuery(id+"F0.wireOp",EDGE,"E77.MirrorCS"),sQuery(id+"F0.wireOp",EDGE,"E78.MirrorCS"),sQuery(id+"F0.wireOp",EDGE,"E79.MirrorCS"),sQuery(id+"F0.wireOp",EDGE,"E80.MirrorCS")])],"isStart":false})});
            var Q20;
            Q20=makeQuery(id+"F3.boolean.opBoolean","COPY",FACE,{"derivedFrom":makeQuery(id+"F3.opExtrude","CAP_FACE",FACE,{"disambiguationData":[OSD([sQuery(id+"F0.wireOp",EDGE,"E81.MirrorCS"),sQuery(id+"F0.wireOp",EDGE,"E82.MirrorCS"),sQuery(id+"F0.wireOp",EDGE,"E83.MirrorCS"),sQuery(id+"F0.wireOp",EDGE,"E84.MirrorCS"),sQuery(id+"F0.wireOp",EDGE,"E85.MirrorCS"),sQuery(id+"F0.wireOp",EDGE,"E86.MirrorCS")])],"isStart":false})});
            fillet(context, id + "F5", {"entities" : qUnion([Q0, Q1, Q2, Q3, Q4, Q5, Q6, Q7, Q8, Q9, Q10, Q11, Q12, Q13, Q14, Q15, Q16, Q17, Q18, Q19, Q20]), "radius" : .5 * mm, "tangentPropagation" : true, "allowEdgeOverflow" : false});
        }
        {
            var Q0;
            Q0=makeQuery(id+"F4.boolean.opBoolean","COPY",EDGE,{"derivedFrom":makeQuery(id+"F4.opExtrude","CAP_EDGE",EDGE,{"disambiguationData":[OSD([sQuery(id+"F0.wireOp",EDGE,"E27.MirrorCS")])],"isStart":true})});
            var Q1;
            Q1=makeQuery(id+"F4.boolean.opBoolean","COPY",EDGE,{"derivedFrom":makeQuery(id+"F4.opExtrude","CAP_EDGE",EDGE,{"disambiguationData":[OSD([sQuery(id+"F0.wireOp",EDGE,"E26.MirrorCS")])],"isStart":true})});
            var Q2;
            Q2=makeQuery(id+"F4.boolean.opBoolean","COPY",EDGE,{"derivedFrom":makeQuery(id+"F4.opExtrude","CAP_EDGE",EDGE,{"disambiguationData":[OSD([sQuery(id+"F0.wireOp",EDGE,"E31.MirrorCS")])],"isStart":true})});
            var Q3;
            Q3=makeQuery(id+"F4.boolean.opBoolean","COPY",EDGE,{"derivedFrom":makeQuery(id+"F4.opExtrude","CAP_EDGE",EDGE,{"disambiguationData":[OSD([sQuery(id+"F0.wireOp",EDGE,"E30.MirrorCS")])],"isStart":true})});
            var Q4;
            Q4=makeQuery(id+"F4.boolean.opBoolean","COPY",EDGE,{"derivedFrom":makeQuery(id+"F4.opExtrude","CAP_EDGE",EDGE,{"disambiguationData":[OSD([sQuery(id+"F0.wireOp",EDGE,"E29.MirrorCS")])],"isStart":true})});
            var Q5;
            Q5=makeQuery(id+"F4.boolean.opBoolean","COPY",EDGE,{"derivedFrom":makeQuery(id+"F4.opExtrude","CAP_EDGE",EDGE,{"disambiguationData":[OSD([sQuery(id+"F0.wireOp",EDGE,"E28.MirrorCS")])],"isStart":true})});
            var Q6;
            Q6=makeQuery(id+"F4.boolean.opBoolean","COPY",EDGE,{"derivedFrom":makeQuery(id+"F4.opExtrude","CAP_EDGE",EDGE,{"disambiguationData":[OSD([sQuery(id+"F0.wireOp",EDGE,"E33.MirrorCS")])],"isStart":true})});
            var Q7;
            Q7=makeQuery(id+"F4.boolean.opBoolean","COPY",EDGE,{"derivedFrom":makeQuery(id+"F4.opExtrude","CAP_EDGE",EDGE,{"disambiguationData":[OSD([sQuery(id+"F0.wireOp",EDGE,"E37.MirrorCS")])],"isStart":true})});
            var Q8;
            Q8=makeQuery(id+"F4.boolean.opBoolean","COPY",EDGE,{"derivedFrom":makeQuery(id+"F4.opExtrude","CAP_EDGE",EDGE,{"disambiguationData":[OSD([sQuery(id+"F0.wireOp",EDGE,"E35.MirrorCS")])],"isStart":true})});
            var Q9;
            Q9=makeQuery(id+"F4.boolean.opBoolean","COPY",EDGE,{"derivedFrom":makeQuery(id+"F4.opExtrude","CAP_EDGE",EDGE,{"disambiguationData":[OSD([sQuery(id+"F0.wireOp",EDGE,"E34.MirrorCS")])],"isStart":true})});
            var Q10;
            Q10=makeQuery(id+"F4.boolean.opBoolean","COPY",EDGE,{"derivedFrom":makeQuery(id+"F4.opExtrude","CAP_EDGE",EDGE,{"disambiguationData":[OSD([sQuery(id+"F0.wireOp",EDGE,"E32.MirrorCS")])],"isStart":true})});
            var Q11;
            Q11=makeQuery(id+"F4.boolean.opBoolean","COPY",EDGE,{"derivedFrom":makeQuery(id+"F4.opExtrude","CAP_EDGE",EDGE,{"disambiguationData":[OSD([sQuery(id+"F0.wireOp",EDGE,"E36.MirrorCS")])],"isStart":true})});
            var Q12;
            Q12=makeQuery(id+"F3.boolean.opBoolean","COPY",EDGE,{"derivedFrom":makeQuery(id+"F3.opExtrude","CAP_EDGE",EDGE,{"disambiguationData":[OSD([sQuery(id+"F0.wireOp",EDGE,"E61.MirrorCS")])],"isStart":true})});
            var Q13;
            Q13=makeQuery(id+"F3.boolean.opBoolean","COPY",EDGE,{"derivedFrom":makeQuery(id+"F3.opExtrude","CAP_EDGE",EDGE,{"disambiguationData":[OSD([sQuery(id+"F0.wireOp",EDGE,"E50.MirrorCS")])],"isStart":true})});
            var Q14;
            Q14=makeQuery(id+"F3.boolean.opBoolean","COPY",EDGE,{"derivedFrom":makeQuery(id+"F3.opExtrude","CAP_EDGE",EDGE,{"disambiguationData":[OSD([sQuery(id+"F0.wireOp",EDGE,"E54.MirrorCS")])],"isStart":true})});
            var Q15;
            Q15=makeQuery(id+"F3.boolean.opBoolean","COPY",EDGE,{"derivedFrom":makeQuery(id+"F3.opExtrude","CAP_EDGE",EDGE,{"disambiguationData":[OSD([sQuery(id+"F0.wireOp",EDGE,"E52.MirrorCS")])],"isStart":true})});
            var Q16;
            Q16=makeQuery(id+"F3.boolean.opBoolean","COPY",EDGE,{"derivedFrom":makeQuery(id+"F3.opExtrude","CAP_EDGE",EDGE,{"disambiguationData":[OSD([sQuery(id+"F0.wireOp",EDGE,"E49.MirrorCS")])],"isStart":true})});
            var Q17;
            Q17=makeQuery(id+"F3.boolean.opBoolean","COPY",EDGE,{"derivedFrom":makeQuery(id+"F3.opExtrude","CAP_EDGE",EDGE,{"disambiguationData":[OSD([sQuery(id+"F0.wireOp",EDGE,"E46.MirrorCS")])],"isStart":true})});
            var Q18;
            Q18=makeQuery(id+"F3.boolean.opBoolean","COPY",EDGE,{"derivedFrom":makeQuery(id+"F3.opExtrude","CAP_EDGE",EDGE,{"disambiguationData":[OSD([sQuery(id+"F0.wireOp",EDGE,"E57.MirrorCS")])],"isStart":true})});
            var Q19;
            Q19=makeQuery(id+"F3.boolean.opBoolean","COPY",EDGE,{"derivedFrom":makeQuery(id+"F3.opExtrude","CAP_EDGE",EDGE,{"disambiguationData":[OSD([sQuery(id+"F0.wireOp",EDGE,"E51.MirrorCS")])],"isStart":true})});
            var Q20;
            Q20=makeQuery(id+"F3.boolean.opBoolean","COPY",EDGE,{"derivedFrom":makeQuery(id+"F3.opExtrude","CAP_EDGE",EDGE,{"disambiguationData":[OSD([sQuery(id+"F0.wireOp",EDGE,"E47.MirrorCS")])],"isStart":true})});
            var Q21;
            Q21=makeQuery(id+"F3.boolean.opBoolean","COPY",EDGE,{"derivedFrom":makeQuery(id+"F3.opExtrude","CAP_EDGE",EDGE,{"disambiguationData":[OSD([sQuery(id+"F0.wireOp",EDGE,"E45.MirrorCS")])],"isStart":true})});
            var Q22;
            Q22=makeQuery(id+"F3.boolean.opBoolean","COPY",EDGE,{"derivedFrom":makeQuery(id+"F3.opExtrude","CAP_EDGE",EDGE,{"disambiguationData":[OSD([sQuery(id+"F0.wireOp",EDGE,"E53.MirrorCS")])],"isStart":true})});
            var Q23;
            Q23=makeQuery(id+"F3.boolean.opBoolean","COPY",EDGE,{"derivedFrom":makeQuery(id+"F3.opExtrude","CAP_EDGE",EDGE,{"disambiguationData":[OSD([sQuery(id+"F0.wireOp",EDGE,"E62.MirrorCS")])],"isStart":true})});
            var Q24;
            Q24=makeQuery(id+"F4.boolean.opBoolean","COPY",EDGE,{"derivedFrom":makeQuery(id+"F4.opExtrude","CAP_EDGE",EDGE,{"disambiguationData":[OSD([sQuery(id+"F0.wireOp",EDGE,"E21.MirrorCS")])],"isStart":true})});
            var Q25;
            Q25=makeQuery(id+"F4.boolean.opBoolean","COPY",EDGE,{"derivedFrom":makeQuery(id+"F4.opExtrude","CAP_EDGE",EDGE,{"disambiguationData":[OSD([sQuery(id+"F0.wireOp",EDGE,"E25.MirrorCS")])],"isStart":true})});
            var Q26;
            Q26=makeQuery(id+"F4.boolean.opBoolean","COPY",EDGE,{"derivedFrom":makeQuery(id+"F4.opExtrude","CAP_EDGE",EDGE,{"disambiguationData":[OSD([sQuery(id+"F0.wireOp",EDGE,"E17.MirrorCS")])],"isStart":true})});
            var Q27;
            Q27=makeQuery(id+"F4.boolean.opBoolean","COPY",EDGE,{"derivedFrom":makeQuery(id+"F4.opExtrude","CAP_EDGE",EDGE,{"disambiguationData":[OSD([sQuery(id+"F0.wireOp",EDGE,"E15.MirrorCS")])],"isStart":true})});
            var Q28;
            Q28=makeQuery(id+"F4.boolean.opBoolean","COPY",EDGE,{"derivedFrom":makeQuery(id+"F4.opExtrude","CAP_EDGE",EDGE,{"disambiguationData":[OSD([sQuery(id+"F0.wireOp",EDGE,"E20.MirrorCS")])],"isStart":true})});
            var Q29;
            Q29=makeQuery(id+"F4.boolean.opBoolean","COPY",EDGE,{"derivedFrom":makeQuery(id+"F4.opExtrude","CAP_EDGE",EDGE,{"disambiguationData":[OSD([sQuery(id+"F0.wireOp",EDGE,"E24.MirrorCS")])],"isStart":true})});
            var Q30;
            Q30=makeQuery(id+"F4.boolean.opBoolean","COPY",EDGE,{"derivedFrom":makeQuery(id+"F4.opExtrude","CAP_EDGE",EDGE,{"disambiguationData":[OSD([sQuery(id+"F0.wireOp",EDGE,"E16.MirrorCS")])],"isStart":true})});
            var Q31;
            Q31=makeQuery(id+"F4.boolean.opBoolean","COPY",EDGE,{"derivedFrom":makeQuery(id+"F4.opExtrude","CAP_EDGE",EDGE,{"disambiguationData":[OSD([sQuery(id+"F0.wireOp",EDGE,"E18.MirrorCS")])],"isStart":true})});
            var Q32;
            Q32=makeQuery(id+"F4.boolean.opBoolean","COPY",EDGE,{"derivedFrom":makeQuery(id+"F4.opExtrude","CAP_EDGE",EDGE,{"disambiguationData":[OSD([sQuery(id+"F0.wireOp",EDGE,"E19.MirrorCS")])],"isStart":true})});
            var Q33;
            Q33=makeQuery(id+"F4.boolean.opBoolean","COPY",EDGE,{"derivedFrom":makeQuery(id+"F4.opExtrude","CAP_EDGE",EDGE,{"disambiguationData":[OSD([sQuery(id+"F0.wireOp",EDGE,"E22.MirrorCS")])],"isStart":true})});
            var Q34;
            Q34=makeQuery(id+"F4.boolean.opBoolean","COPY",EDGE,{"derivedFrom":makeQuery(id+"F4.opExtrude","CAP_EDGE",EDGE,{"disambiguationData":[OSD([sQuery(id+"F0.wireOp",EDGE,"E14.MirrorCS")])],"isStart":true})});
            var Q35;
            Q35=makeQuery(id+"F4.boolean.opBoolean","COPY",EDGE,{"derivedFrom":makeQuery(id+"F4.opExtrude","CAP_EDGE",EDGE,{"disambiguationData":[OSD([sQuery(id+"F0.wireOp",EDGE,"E23.MirrorCS")])],"isStart":true})});
            var Q36;
            Q36=makeQuery(id+"F3.boolean.opBoolean","COPY",EDGE,{"derivedFrom":makeQuery(id+"F3.opExtrude","CAP_EDGE",EDGE,{"disambiguationData":[OSD([sQuery(id+"F0.wireOp",EDGE,"E55.MirrorCS")])],"isStart":true})});
            var Q37;
            Q37=makeQuery(id+"F3.boolean.opBoolean","COPY",EDGE,{"derivedFrom":makeQuery(id+"F3.opExtrude","CAP_EDGE",EDGE,{"disambiguationData":[OSD([sQuery(id+"F0.wireOp",EDGE,"E48.MirrorCS")])],"isStart":true})});
            var Q38;
            Q38=makeQuery(id+"F3.boolean.opBoolean","COPY",EDGE,{"derivedFrom":makeQuery(id+"F3.opExtrude","CAP_EDGE",EDGE,{"disambiguationData":[OSD([sQuery(id+"F0.wireOp",EDGE,"E59.MirrorCS")])],"isStart":true})});
            var Q39;
            Q39=makeQuery(id+"F4.boolean.opBoolean","COPY",EDGE,{"derivedFrom":makeQuery(id+"F4.opExtrude","CAP_EDGE",EDGE,{"disambiguationData":[OSD([sQuery(id+"F0.wireOp",EDGE,"E38.MirrorCS")])],"isStart":true})});
            var Q40;
            Q40=makeQuery(id+"F4.boolean.opBoolean","COPY",EDGE,{"derivedFrom":makeQuery(id+"F4.opExtrude","CAP_EDGE",EDGE,{"disambiguationData":[OSD([sQuery(id+"F0.wireOp",EDGE,"E12.MirrorCS")])],"isStart":true})});
            var Q41;
            Q41=makeQuery(id+"F4.boolean.opBoolean","COPY",EDGE,{"derivedFrom":makeQuery(id+"F4.opExtrude","CAP_EDGE",EDGE,{"disambiguationData":[OSD([sQuery(id+"F0.wireOp",EDGE,"E42.MirrorCS")])],"isStart":true})});
            var Q42;
            Q42=makeQuery(id+"F4.boolean.opBoolean","COPY",EDGE,{"derivedFrom":makeQuery(id+"F4.opExtrude","CAP_EDGE",EDGE,{"disambiguationData":[OSD([sQuery(id+"F0.wireOp",EDGE,"E9.MirrorCS")])],"isStart":true})});
            var Q43;
            Q43=makeQuery(id+"F4.boolean.opBoolean","COPY",EDGE,{"derivedFrom":makeQuery(id+"F4.opExtrude","CAP_EDGE",EDGE,{"disambiguationData":[OSD([sQuery(id+"F0.wireOp",EDGE,"E8.MirrorCS")])],"isStart":true})});
            var Q44;
            Q44=makeQuery(id+"F4.boolean.opBoolean","COPY",EDGE,{"derivedFrom":makeQuery(id+"F4.opExtrude","CAP_EDGE",EDGE,{"disambiguationData":[OSD([sQuery(id+"F0.wireOp",EDGE,"E40.MirrorCS")])],"isStart":true})});
            var Q45;
            Q45=makeQuery(id+"F4.boolean.opBoolean","COPY",EDGE,{"derivedFrom":makeQuery(id+"F4.opExtrude","CAP_EDGE",EDGE,{"disambiguationData":[OSD([sQuery(id+"F0.wireOp",EDGE,"E10.MirrorCS")])],"isStart":true})});
            var Q46;
            Q46=makeQuery(id+"F4.boolean.opBoolean","COPY",EDGE,{"derivedFrom":makeQuery(id+"F4.opExtrude","CAP_EDGE",EDGE,{"disambiguationData":[OSD([sQuery(id+"F0.wireOp",EDGE,"E13.MirrorCS")])],"isStart":true})});
            var Q47;
            Q47=makeQuery(id+"F4.boolean.opBoolean","COPY",EDGE,{"derivedFrom":makeQuery(id+"F4.opExtrude","CAP_EDGE",EDGE,{"disambiguationData":[OSD([sQuery(id+"F0.wireOp",EDGE,"E43.MirrorCS")])],"isStart":true})});
            var Q48;
            Q48=makeQuery(id+"F3.boolean.opBoolean","COPY",EDGE,{"derivedFrom":makeQuery(id+"F3.opExtrude","CAP_EDGE",EDGE,{"disambiguationData":[OSD([sQuery(id+"F0.wireOp",EDGE,"E60.MirrorCS")])],"isStart":true})});
            var Q49;
            Q49=makeQuery(id+"F3.boolean.opBoolean","COPY",EDGE,{"derivedFrom":makeQuery(id+"F3.opExtrude","CAP_EDGE",EDGE,{"disambiguationData":[OSD([sQuery(id+"F0.wireOp",EDGE,"E58.MirrorCS")])],"isStart":true})});
            var Q50;
            Q50=makeQuery(id+"F3.boolean.opBoolean","COPY",EDGE,{"derivedFrom":makeQuery(id+"F3.opExtrude","CAP_EDGE",EDGE,{"disambiguationData":[OSD([sQuery(id+"F0.wireOp",EDGE,"E56.MirrorCS")])],"isStart":true})});
            var Q51;
            Q51=makeQuery(id+"F4.boolean.opBoolean","COPY",EDGE,{"derivedFrom":makeQuery(id+"F4.opExtrude","CAP_EDGE",EDGE,{"disambiguationData":[OSD([sQuery(id+"F0.wireOp",EDGE,"E41.MirrorCS")])],"isStart":true})});
            var Q52;
            Q52=makeQuery(id+"F4.boolean.opBoolean","COPY",EDGE,{"derivedFrom":makeQuery(id+"F4.opExtrude","CAP_EDGE",EDGE,{"disambiguationData":[OSD([sQuery(id+"F0.wireOp",EDGE,"E39.MirrorCS")])],"isStart":true})});
            var Q53;
            Q53=makeQuery(id+"F4.boolean.opBoolean","COPY",EDGE,{"derivedFrom":makeQuery(id+"F4.opExtrude","CAP_EDGE",EDGE,{"disambiguationData":[OSD([sQuery(id+"F0.wireOp",EDGE,"E11.MirrorCS")])],"isStart":true})});
            var Q54;
            Q54=makeQuery(id+"F4.boolean.opBoolean","COPY",EDGE,{"derivedFrom":makeQuery(id+"F4.opExtrude","CAP_EDGE",EDGE,{"disambiguationData":[OSD([sQuery(id+"F0.wireOp",EDGE,"E6.0.1.0")])],"isStart":true})});
            var Q55;
            Q55=makeQuery(id+"F4.boolean.opBoolean","COPY",EDGE,{"derivedFrom":makeQuery(id+"F4.opExtrude","CAP_EDGE",EDGE,{"disambiguationData":[OSD([sQuery(id+"F0.wireOp",EDGE,"E6.0.1.7")])],"isStart":true})});
            var Q56;
            Q56=makeQuery(id+"F4.boolean.opBoolean","COPY",EDGE,{"derivedFrom":makeQuery(id+"F4.opExtrude","CAP_EDGE",EDGE,{"disambiguationData":[OSD([sQuery(id+"F0.wireOp",EDGE,"E6.0.1.5")])],"isStart":true})});
            var Q57;
            Q57=makeQuery(id+"F3.boolean.opBoolean","COPY",EDGE,{"derivedFrom":makeQuery(id+"F3.opExtrude","CAP_EDGE",EDGE,{"disambiguationData":[OSD([sQuery(id+"F0.wireOp",EDGE,"E65.MirrorCS")])],"isStart":true})});
            var Q58;
            Q58=makeQuery(id+"F3.boolean.opBoolean","COPY",EDGE,{"derivedFrom":makeQuery(id+"F3.opExtrude","CAP_EDGE",EDGE,{"disambiguationData":[OSD([sQuery(id+"F0.wireOp",EDGE,"E66.MirrorCS")])],"isStart":true})});
            var Q59;
            Q59=makeQuery(id+"F3.boolean.opBoolean","COPY",EDGE,{"derivedFrom":makeQuery(id+"F3.opExtrude","CAP_EDGE",EDGE,{"disambiguationData":[OSD([sQuery(id+"F0.wireOp",EDGE,"E67.MirrorCS")])],"isStart":true})});
            var Q60;
            Q60=makeQuery(id+"F3.boolean.opBoolean","COPY",EDGE,{"derivedFrom":makeQuery(id+"F3.opExtrude","CAP_EDGE",EDGE,{"disambiguationData":[OSD([sQuery(id+"F0.wireOp",EDGE,"E68.MirrorCS")])],"isStart":true})});
            var Q61;
            Q61=makeQuery(id+"F3.boolean.opBoolean","COPY",EDGE,{"derivedFrom":makeQuery(id+"F3.opExtrude","CAP_EDGE",EDGE,{"disambiguationData":[OSD([sQuery(id+"F0.wireOp",EDGE,"E73.MirrorCS")])],"isStart":true})});
            var Q62;
            Q62=makeQuery(id+"F4.boolean.opBoolean","COPY",EDGE,{"derivedFrom":makeQuery(id+"F4.opExtrude","CAP_EDGE",EDGE,{"disambiguationData":[OSD([sQuery(id+"F0.wireOp",EDGE,"E6.1.1.0")])],"isStart":true})});
            var Q63;
            Q63=makeQuery(id+"F4.boolean.opBoolean","COPY",EDGE,{"derivedFrom":makeQuery(id+"F4.opExtrude","CAP_EDGE",EDGE,{"disambiguationData":[OSD([sQuery(id+"F0.wireOp",EDGE,"E6.1.1.1")])],"isStart":true})});
            var Q64;
            Q64=makeQuery(id+"F4.boolean.opBoolean","COPY",EDGE,{"derivedFrom":makeQuery(id+"F4.opExtrude","CAP_EDGE",EDGE,{"disambiguationData":[OSD([sQuery(id+"F0.wireOp",EDGE,"E5.3")])],"isStart":true})});
            var Q65;
            Q65=makeQuery(id+"F3.boolean.opBoolean","COPY",EDGE,{"derivedFrom":makeQuery(id+"F3.opExtrude","CAP_EDGE",EDGE,{"disambiguationData":[OSD([sQuery(id+"F0.wireOp",EDGE,"E69.MirrorCS")])],"isStart":true})});
            var Q66;
            Q66=makeQuery(id+"F4.boolean.opBoolean","COPY",EDGE,{"derivedFrom":makeQuery(id+"F4.opExtrude","CAP_EDGE",EDGE,{"disambiguationData":[OSD([sQuery(id+"F0.wireOp",EDGE,"E5.1")])],"isStart":true})});
            var Q67;
            Q67=makeQuery(id+"F4.boolean.opBoolean","COPY",EDGE,{"derivedFrom":makeQuery(id+"F4.opExtrude","CAP_EDGE",EDGE,{"disambiguationData":[OSD([sQuery(id+"F0.wireOp",EDGE,"E6.0.1.2")])],"isStart":true})});
            var Q68;
            Q68=makeQuery(id+"F4.boolean.opBoolean","COPY",EDGE,{"derivedFrom":makeQuery(id+"F4.opExtrude","CAP_EDGE",EDGE,{"disambiguationData":[OSD([sQuery(id+"F0.wireOp",EDGE,"E6.1.0.7")])],"isStart":true})});
            var Q69;
            Q69=makeQuery(id+"F4.boolean.opBoolean","COPY",EDGE,{"derivedFrom":makeQuery(id+"F4.opExtrude","CAP_EDGE",EDGE,{"disambiguationData":[OSD([sQuery(id+"F0.wireOp",EDGE,"E6.1.0.2")])],"isStart":true})});
            var Q70;
            Q70=makeQuery(id+"F4.boolean.opBoolean","COPY",EDGE,{"derivedFrom":makeQuery(id+"F4.opExtrude","CAP_EDGE",EDGE,{"disambiguationData":[OSD([sQuery(id+"F0.wireOp",EDGE,"E6.1.1.4")])],"isStart":true})});
            var Q71;
            Q71=makeQuery(id+"F4.boolean.opBoolean","COPY",EDGE,{"derivedFrom":makeQuery(id+"F4.opExtrude","CAP_EDGE",EDGE,{"disambiguationData":[OSD([sQuery(id+"F0.wireOp",EDGE,"E6.1.1.5")])],"isStart":true})});
            var Q72;
            Q72=makeQuery(id+"F4.boolean.opBoolean","COPY",EDGE,{"derivedFrom":makeQuery(id+"F4.opExtrude","CAP_EDGE",EDGE,{"disambiguationData":[OSD([sQuery(id+"F0.wireOp",EDGE,"E6.1.0.0")])],"isStart":true})});
            var Q73;
            Q73=makeQuery(id+"F4.boolean.opBoolean","COPY",EDGE,{"derivedFrom":makeQuery(id+"F4.opExtrude","CAP_EDGE",EDGE,{"disambiguationData":[OSD([sQuery(id+"F0.wireOp",EDGE,"E6.0.1.1")])],"isStart":true})});
            var Q74;
            Q74=makeQuery(id+"F3.boolean.opBoolean","COPY",EDGE,{"derivedFrom":makeQuery(id+"F3.opExtrude","CAP_EDGE",EDGE,{"disambiguationData":[OSD([sQuery(id+"F0.wireOp",EDGE,"E63.MirrorCS")])],"isStart":true})});
            var Q75;
            Q75=makeQuery(id+"F4.boolean.opBoolean","COPY",EDGE,{"derivedFrom":makeQuery(id+"F4.opExtrude","CAP_EDGE",EDGE,{"disambiguationData":[OSD([sQuery(id+"F0.wireOp",EDGE,"E6.1.1.2")])],"isStart":true})});
            var Q76;
            Q76=makeQuery(id+"F4.boolean.opBoolean","COPY",EDGE,{"derivedFrom":makeQuery(id+"F4.opExtrude","CAP_EDGE",EDGE,{"disambiguationData":[OSD([sQuery(id+"F0.wireOp",EDGE,"E6.0.1.4")])],"isStart":true})});
            var Q77;
            Q77=makeQuery(id+"F4.boolean.opBoolean","COPY",EDGE,{"derivedFrom":makeQuery(id+"F4.opExtrude","CAP_EDGE",EDGE,{"disambiguationData":[OSD([sQuery(id+"F0.wireOp",EDGE,"E6.1.1.7")])],"isStart":true})});
            var Q78;
            Q78=makeQuery(id+"F4.boolean.opBoolean","COPY",EDGE,{"derivedFrom":makeQuery(id+"F4.opExtrude","CAP_EDGE",EDGE,{"disambiguationData":[OSD([sQuery(id+"F0.wireOp",EDGE,"E5.4")])],"isStart":true})});
            var Q79;
            Q79=makeQuery(id+"F3.boolean.opBoolean","COPY",EDGE,{"derivedFrom":makeQuery(id+"F3.opExtrude","CAP_EDGE",EDGE,{"disambiguationData":[OSD([sQuery(id+"F0.wireOp",EDGE,"E74.MirrorCS")])],"isStart":true})});
            var Q80;
            Q80=makeQuery(id+"F4.boolean.opBoolean","COPY",EDGE,{"derivedFrom":makeQuery(id+"F4.opExtrude","CAP_EDGE",EDGE,{"disambiguationData":[OSD([sQuery(id+"F0.wireOp",EDGE,"E5.0")])],"isStart":true})});
            var Q81;
            Q81=makeQuery(id+"F4.boolean.opBoolean","COPY",EDGE,{"derivedFrom":makeQuery(id+"F4.opExtrude","CAP_EDGE",EDGE,{"disambiguationData":[OSD([sQuery(id+"F0.wireOp",EDGE,"E5.2")])],"isStart":true})});
            var Q82;
            Q82=makeQuery(id+"F3.boolean.opBoolean","COPY",EDGE,{"derivedFrom":makeQuery(id+"F3.opExtrude","CAP_EDGE",EDGE,{"disambiguationData":[OSD([sQuery(id+"F0.wireOp",EDGE,"E70.MirrorCS")])],"isStart":true})});
            var Q83;
            Q83=makeQuery(id+"F3.boolean.opBoolean","COPY",EDGE,{"derivedFrom":makeQuery(id+"F3.opExtrude","CAP_EDGE",EDGE,{"disambiguationData":[OSD([sQuery(id+"F0.wireOp",EDGE,"E72.MirrorCS")])],"isStart":true})});
            var Q84;
            Q84=makeQuery(id+"F3.boolean.opBoolean","COPY",EDGE,{"derivedFrom":makeQuery(id+"F3.opExtrude","CAP_EDGE",EDGE,{"disambiguationData":[OSD([sQuery(id+"F0.wireOp",EDGE,"E64.MirrorCS")])],"isStart":true})});
            var Q85;
            Q85=makeQuery(id+"F4.boolean.opBoolean","COPY",EDGE,{"derivedFrom":makeQuery(id+"F4.opExtrude","CAP_EDGE",EDGE,{"disambiguationData":[OSD([sQuery(id+"F0.wireOp",EDGE,"E6.1.0.4")])],"isStart":true})});
            var Q86;
            Q86=makeQuery(id+"F3.boolean.opBoolean","COPY",EDGE,{"derivedFrom":makeQuery(id+"F3.opExtrude","CAP_EDGE",EDGE,{"disambiguationData":[OSD([sQuery(id+"F0.wireOp",EDGE,"E71.MirrorCS")])],"isStart":true})});
            var Q87;
            Q87=makeQuery(id+"F4.boolean.opBoolean","COPY",EDGE,{"derivedFrom":makeQuery(id+"F4.opExtrude","CAP_EDGE",EDGE,{"disambiguationData":[OSD([sQuery(id+"F0.wireOp",EDGE,"E6.1.0.5")])],"isStart":true})});
            var Q88;
            Q88=makeQuery(id+"F4.boolean.opBoolean","COPY",EDGE,{"derivedFrom":makeQuery(id+"F4.opExtrude","CAP_EDGE",EDGE,{"disambiguationData":[OSD([sQuery(id+"F0.wireOp",EDGE,"E6.1.0.1")])],"isStart":true})});
            var Q89;
            Q89=makeQuery(id+"F4.boolean.opBoolean","COPY",EDGE,{"derivedFrom":makeQuery(id+"F4.opExtrude","CAP_EDGE",EDGE,{"disambiguationData":[OSD([sQuery(id+"F0.wireOp",EDGE,"E5.5")])],"isStart":true})});
            var Q90;
            Q90=makeQuery(id+"F2.opExtrude","SWEPT_FACE",FACE,{"disambiguationData":[OSD([sQuery(id+"F1.wireOp",EDGE,"E92.0")])]});
            var Q91;
            Q91=makeQuery(id+"F3.boolean.opBoolean","COPY",EDGE,{"derivedFrom":makeQuery(id+"F3.opExtrude","CAP_EDGE",EDGE,{"disambiguationData":[OSD([sQuery(id+"F0.wireOp",EDGE,"E84.MirrorCS")])],"isStart":true})});
            var Q92;
            Q92=makeQuery(id+"F4.boolean.opBoolean","COPY",EDGE,{"derivedFrom":makeQuery(id+"F4.opExtrude","CAP_EDGE",EDGE,{"disambiguationData":[OSD([sQuery(id+"F0.wireOp",EDGE,"E6.3.1.5")])],"isStart":true})});
            var Q93;
            Q93=makeQuery(id+"F4.boolean.opBoolean","COPY",EDGE,{"derivedFrom":makeQuery(id+"F4.opExtrude","CAP_EDGE",EDGE,{"disambiguationData":[OSD([sQuery(id+"F0.wireOp",EDGE,"E6.2.1.2")])],"isStart":true})});
            var Q94;
            Q94=makeQuery(id+"F4.boolean.opBoolean","COPY",EDGE,{"derivedFrom":makeQuery(id+"F4.opExtrude","CAP_EDGE",EDGE,{"disambiguationData":[OSD([sQuery(id+"F0.wireOp",EDGE,"E6.3.0.0")])],"isStart":true})});
            var Q95;
            Q95=makeQuery(id+"F3.boolean.opBoolean","COPY",EDGE,{"derivedFrom":makeQuery(id+"F3.opExtrude","CAP_EDGE",EDGE,{"disambiguationData":[OSD([sQuery(id+"F0.wireOp",EDGE,"E82.MirrorCS")])],"isStart":true})});
            var Q96;
            Q96=makeQuery(id+"F4.boolean.opBoolean","COPY",EDGE,{"derivedFrom":makeQuery(id+"F4.opExtrude","CAP_EDGE",EDGE,{"disambiguationData":[OSD([sQuery(id+"F0.wireOp",EDGE,"E6.2.0.2")])],"isStart":true})});
            var Q97;
            Q97=makeQuery(id+"F4.boolean.opBoolean","COPY",EDGE,{"derivedFrom":makeQuery(id+"F4.opExtrude","CAP_EDGE",EDGE,{"disambiguationData":[OSD([sQuery(id+"F0.wireOp",EDGE,"E6.2.0.5")])],"isStart":true})});
            var Q98;
            Q98=makeQuery(id+"F3.boolean.opBoolean","COPY",EDGE,{"derivedFrom":makeQuery(id+"F3.opExtrude","CAP_EDGE",EDGE,{"disambiguationData":[OSD([sQuery(id+"F0.wireOp",EDGE,"E80.MirrorCS")])],"isStart":true})});
            var Q99;
            Q99=makeQuery(id+"F4.boolean.opBoolean","COPY",EDGE,{"derivedFrom":makeQuery(id+"F4.opExtrude","CAP_EDGE",EDGE,{"disambiguationData":[OSD([sQuery(id+"F0.wireOp",EDGE,"E6.2.1.7")])],"isStart":true})});
            var Q100;
            Q100=makeQuery(id+"F3.boolean.opBoolean","COPY",EDGE,{"derivedFrom":makeQuery(id+"F3.opExtrude","CAP_EDGE",EDGE,{"disambiguationData":[OSD([sQuery(id+"F0.wireOp",EDGE,"E77.MirrorCS")])],"isStart":true})});
            var Q101;
            Q101=makeQuery(id+"F4.boolean.opBoolean","COPY",EDGE,{"derivedFrom":makeQuery(id+"F4.opExtrude","CAP_EDGE",EDGE,{"disambiguationData":[OSD([sQuery(id+"F0.wireOp",EDGE,"E6.2.0.0")])],"isStart":true})});
            var Q102;
            Q102=makeQuery(id+"F4.boolean.opBoolean","COPY",EDGE,{"derivedFrom":makeQuery(id+"F4.opExtrude","CAP_EDGE",EDGE,{"disambiguationData":[OSD([sQuery(id+"F0.wireOp",EDGE,"E6.3.1.0")])],"isStart":true})});
            var Q103;
            Q103=makeQuery(id+"F3.boolean.opBoolean","COPY",EDGE,{"derivedFrom":makeQuery(id+"F3.opExtrude","CAP_EDGE",EDGE,{"disambiguationData":[OSD([sQuery(id+"F0.wireOp",EDGE,"E78.MirrorCS")])],"isStart":true})});
            var Q104;
            Q104=makeQuery(id+"F4.boolean.opBoolean","COPY",EDGE,{"derivedFrom":makeQuery(id+"F4.opExtrude","CAP_EDGE",EDGE,{"disambiguationData":[OSD([sQuery(id+"F0.wireOp",EDGE,"E6.2.1.0")])],"isStart":true})});
            var Q105;
            Q105=makeQuery(id+"F4.boolean.opBoolean","COPY",EDGE,{"derivedFrom":makeQuery(id+"F4.opExtrude","CAP_EDGE",EDGE,{"disambiguationData":[OSD([sQuery(id+"F0.wireOp",EDGE,"E6.3.0.1")])],"isStart":true})});
            var Q106;
            Q106=makeQuery(id+"F4.boolean.opBoolean","COPY",EDGE,{"derivedFrom":makeQuery(id+"F4.opExtrude","CAP_EDGE",EDGE,{"disambiguationData":[OSD([sQuery(id+"F0.wireOp",EDGE,"E6.2.0.1")])],"isStart":true})});
            var Q107;
            Q107=makeQuery(id+"F4.boolean.opBoolean","COPY",EDGE,{"derivedFrom":makeQuery(id+"F4.opExtrude","CAP_EDGE",EDGE,{"disambiguationData":[OSD([sQuery(id+"F0.wireOp",EDGE,"E6.2.1.5")])],"isStart":true})});
            var Q108;
            Q108=makeQuery(id+"F3.boolean.opBoolean","COPY",EDGE,{"derivedFrom":makeQuery(id+"F3.opExtrude","CAP_EDGE",EDGE,{"disambiguationData":[OSD([sQuery(id+"F0.wireOp",EDGE,"E81.MirrorCS")])],"isStart":true})});
            var Q109;
            Q109=makeQuery(id+"F4.boolean.opBoolean","COPY",EDGE,{"derivedFrom":makeQuery(id+"F4.opExtrude","CAP_EDGE",EDGE,{"disambiguationData":[OSD([sQuery(id+"F0.wireOp",EDGE,"E6.3.0.5")])],"isStart":true})});
            var Q110;
            Q110=makeQuery(id+"F3.boolean.opBoolean","COPY",EDGE,{"derivedFrom":makeQuery(id+"F3.opExtrude","CAP_EDGE",EDGE,{"disambiguationData":[OSD([sQuery(id+"F0.wireOp",EDGE,"E83.MirrorCS")])],"isStart":true})});
            var Q111;
            Q111=makeQuery(id+"F4.boolean.opBoolean","COPY",EDGE,{"derivedFrom":makeQuery(id+"F4.opExtrude","CAP_EDGE",EDGE,{"disambiguationData":[OSD([sQuery(id+"F0.wireOp",EDGE,"E6.3.0.4")])],"isStart":true})});
            var Q112;
            Q112=makeQuery(id+"F4.boolean.opBoolean","COPY",EDGE,{"derivedFrom":makeQuery(id+"F4.opExtrude","CAP_EDGE",EDGE,{"disambiguationData":[OSD([sQuery(id+"F0.wireOp",EDGE,"E6.2.0.4")])],"isStart":true})});
            var Q113;
            Q113=makeQuery(id+"F4.boolean.opBoolean","COPY",EDGE,{"derivedFrom":makeQuery(id+"F4.opExtrude","CAP_EDGE",EDGE,{"disambiguationData":[OSD([sQuery(id+"F0.wireOp",EDGE,"E6.3.0.2")])],"isStart":true})});
            var Q114;
            Q114=makeQuery(id+"F4.boolean.opBoolean","COPY",EDGE,{"derivedFrom":makeQuery(id+"F4.opExtrude","CAP_EDGE",EDGE,{"disambiguationData":[OSD([sQuery(id+"F0.wireOp",EDGE,"E6.2.1.4")])],"isStart":true})});
            var Q115;
            Q115=makeQuery(id+"F4.boolean.opBoolean","COPY",EDGE,{"derivedFrom":makeQuery(id+"F4.opExtrude","CAP_EDGE",EDGE,{"disambiguationData":[OSD([sQuery(id+"F0.wireOp",EDGE,"E6.3.1.2")])],"isStart":true})});
            var Q116;
            Q116=makeQuery(id+"F3.boolean.opBoolean","COPY",EDGE,{"derivedFrom":makeQuery(id+"F3.opExtrude","CAP_EDGE",EDGE,{"disambiguationData":[OSD([sQuery(id+"F0.wireOp",EDGE,"E85.MirrorCS")])],"isStart":true})});
            var Q117;
            Q117=makeQuery(id+"F3.boolean.opBoolean","COPY",EDGE,{"derivedFrom":makeQuery(id+"F3.opExtrude","CAP_EDGE",EDGE,{"disambiguationData":[OSD([sQuery(id+"F0.wireOp",EDGE,"E79.MirrorCS")])],"isStart":true})});
            var Q118;
            Q118=makeQuery(id+"F3.boolean.opBoolean","COPY",EDGE,{"derivedFrom":makeQuery(id+"F3.opExtrude","CAP_EDGE",EDGE,{"disambiguationData":[OSD([sQuery(id+"F0.wireOp",EDGE,"E75.MirrorCS")])],"isStart":true})});
            var Q119;
            Q119=makeQuery(id+"F4.boolean.opBoolean","COPY",EDGE,{"derivedFrom":makeQuery(id+"F4.opExtrude","CAP_EDGE",EDGE,{"disambiguationData":[OSD([sQuery(id+"F0.wireOp",EDGE,"E6.3.1.1")])],"isStart":true})});
            var Q120;
            Q120=makeQuery(id+"F3.boolean.opBoolean","COPY",EDGE,{"derivedFrom":makeQuery(id+"F3.opExtrude","CAP_EDGE",EDGE,{"disambiguationData":[OSD([sQuery(id+"F0.wireOp",EDGE,"E76.MirrorCS")])],"isStart":true})});
            var Q121;
            Q121=makeQuery(id+"F4.boolean.opBoolean","COPY",EDGE,{"derivedFrom":makeQuery(id+"F4.opExtrude","CAP_EDGE",EDGE,{"disambiguationData":[OSD([sQuery(id+"F0.wireOp",EDGE,"E6.3.0.7")])],"isStart":true})});
            var Q122;
            Q122=makeQuery(id+"F4.boolean.opBoolean","COPY",EDGE,{"derivedFrom":makeQuery(id+"F4.opExtrude","CAP_EDGE",EDGE,{"disambiguationData":[OSD([sQuery(id+"F0.wireOp",EDGE,"E6.3.1.7")])],"isStart":true})});
            var Q123;
            Q123=makeQuery(id+"F4.boolean.opBoolean","COPY",EDGE,{"derivedFrom":makeQuery(id+"F4.opExtrude","CAP_EDGE",EDGE,{"disambiguationData":[OSD([sQuery(id+"F0.wireOp",EDGE,"E6.2.1.1")])],"isStart":true})});
            var Q124;
            Q124=makeQuery(id+"F4.boolean.opBoolean","COPY",EDGE,{"derivedFrom":makeQuery(id+"F4.opExtrude","CAP_EDGE",EDGE,{"disambiguationData":[OSD([sQuery(id+"F0.wireOp",EDGE,"E6.2.0.7")])],"isStart":true})});
            var Q125;
            Q125=makeQuery(id+"F4.boolean.opBoolean","COPY",EDGE,{"derivedFrom":makeQuery(id+"F4.opExtrude","CAP_EDGE",EDGE,{"disambiguationData":[OSD([sQuery(id+"F0.wireOp",EDGE,"E6.3.1.4")])],"isStart":true})});
            var Q126;
            Q126=makeQuery(id+"F3.boolean.opBoolean","COPY",EDGE,{"derivedFrom":makeQuery(id+"F3.opExtrude","CAP_EDGE",EDGE,{"disambiguationData":[OSD([sQuery(id+"F0.wireOp",EDGE,"E86.MirrorCS")])],"isStart":true})});
            fillet(context, id + "F6", {"entities" : qUnion([Q0, Q1, Q2, Q3, Q4, Q5, Q6, Q7, Q8, Q9, Q10, Q11, Q12, Q13, Q14, Q15, Q16, Q17, Q18, Q19, Q20, Q21, Q22, Q23, Q24, Q25, Q26, Q27, Q28, Q29, Q30, Q31, Q32, Q33, Q34, Q35, Q36, Q37, Q38, Q39, Q40, Q41, Q42, Q43, Q44, Q45, Q46, Q47, Q48, Q49, Q50, Q51, Q52, Q53, Q54, Q55, Q56, Q57, Q58, Q59, Q60, Q61, Q62, Q63, Q64, Q65, Q66, Q67, Q68, Q69, Q70, Q71, Q72, Q73, Q74, Q75, Q76, Q77, Q78, Q79, Q80, Q81, Q82, Q83, Q84, Q85, Q86, Q87, Q88, Q89, Q90, Q91, Q92, Q93, Q94, Q95, Q96, Q97, Q98, Q99, Q100, Q101, Q102, Q103, Q104, Q105, Q106, Q107, Q108, Q109, Q110, Q111, Q112, Q113, Q114, Q115, Q116, Q117, Q118, Q119, Q120, Q121, Q122, Q123, Q124, Q125, Q126]), "radius" : .75 * mm, "tangentPropagation" : true, "allowEdgeOverflow" : false});
        }
        {
            var Q0;
            Q0=makeQuery(id+"F2.opExtrude","SWEPT_FACE",FACE,{"disambiguationData":[OSD([sQuery(id+"F1.wireOp",EDGE,"E90.0")])]});
            var sketch = newSketch(context, id + "F7", { "sketchPlane" : qUnion([Q0])});
            skText(sketch, "E95", { "text": "Bottino\n02-18-17", "fontName": "OpenSans-Bold.ttf"});
            const initialGuessF7  = {"E95": [-0.0137, -0.00788, 1, 0, 0.0048]};
            skSetInitialGuess(sketch, initialGuessF7);
            skSolve(sketch);
        }
        {
            var Q0;
            Q0 = qSketchRegion(id + "F7", true);
            extrude(context, id + "F8", {"entities" : qUnion([Q0]), "operationType" : NewBodyOperationType.REMOVE, "oppositeDirection" : true, "depth" : 1 * mm, "offsetDistance" : 25 * mm});
        }
    });
